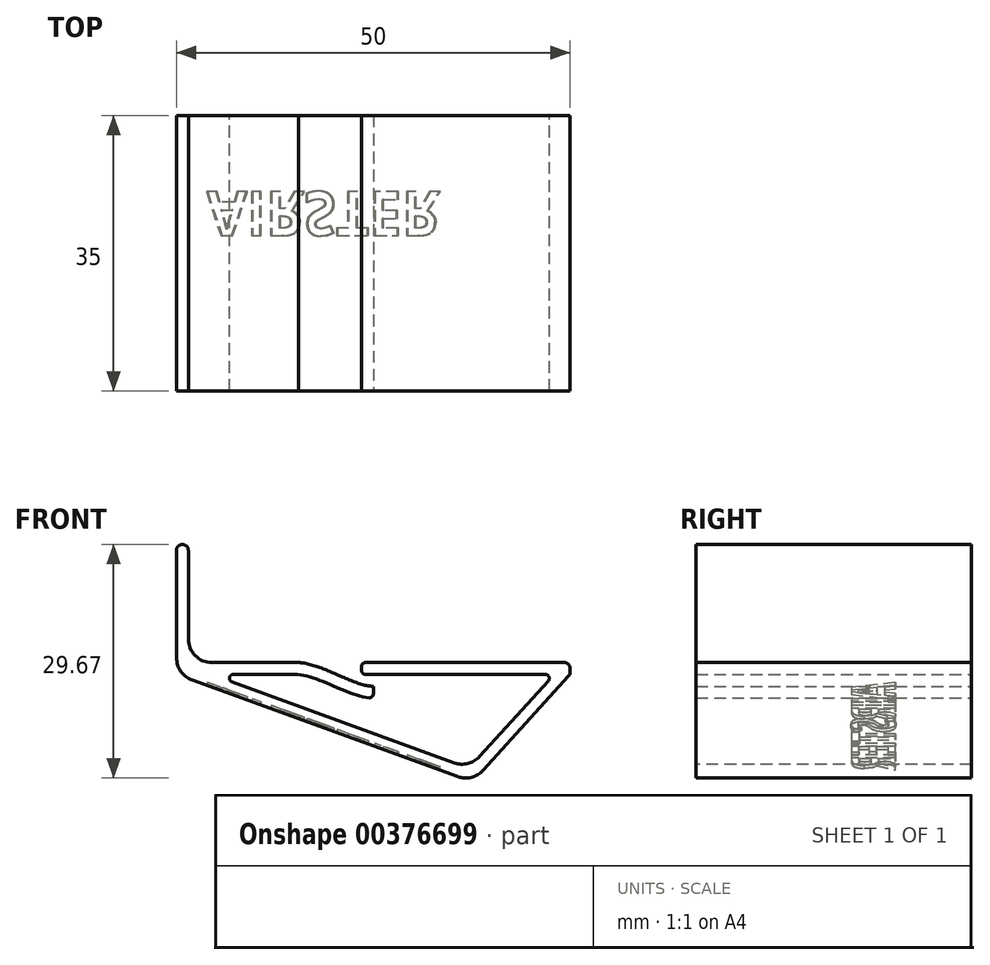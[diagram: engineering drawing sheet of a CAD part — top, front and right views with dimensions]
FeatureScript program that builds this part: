
annotation { "Feature Type Name" : "Feature", "Feature Type Description" : "" }
export const myFeature = defineFeature(function(context is Context, id is Id, definition is map)
    precondition{}
    {
        {
            var Q0;
            Q0=qCreatedBy(makeId("Front.planeOp"),FACE);
            var sketch = newSketch(context, id + "F0", { "sketchPlane" : qUnion([Q0])});
            skLineSegment(sketch, "E0.bottom", {"start": v(0, 1.5) * mm, "end": v(50, 1.5) * mm});
            skLineSegment(sketch, "E0.top", {"start": v(0, 0) * mm, "end": v(50, 0) * mm});
            skLineSegment(sketch, "E0.left", {"start": v(0, 1.5) * mm, "end": v(0, 0) * mm});
            skLineSegment(sketch, "E0.right", {"start": v(50, 1.5) * mm, "end": v(50, 0) * mm});
            skLineSegment(sketch, "E1.bottom", {"start": v(0, 16.5) * mm, "end": v(1.5, 16.5) * mm});
            skLineSegment(sketch, "E1.top", {"start": v(0, 1.5) * mm, "end": v(1.5, 1.5) * mm});
            skLineSegment(sketch, "E1.left", {"start": v(0, 16.5) * mm, "end": v(0, 1.5) * mm});
            skLineSegment(sketch, "E1.right", {"start": v(1.5, 16.5) * mm, "end": v(1.5, 1.5) * mm});
            skFitSpline(sketch, "E2", {"points": [v(25, -3) * mm, v(15, 0) * mm], "startDerivative": vector(-9, 0) * mm, "endDerivative": vector(-9, 0) * mm});
            skLineSegment(sketch, "E3", {"start": v(0, 0) * mm, "end": v(37.59, -13.68) * mm});
            skLineSegment(sketch, "E4", {"start": v(4.39, 0) * mm, "end": v(38.1, -12.27) * mm});
            skLineSegment(sketch, "E5", {"start": v(37.59, -13.68) * mm, "end": v(38.1, -12.27) * mm});
            skLineSegment(sketch, "E6", {"start": v(37.59, -13.68) * mm, "end": v(50, 0) * mm});
            skLineSegment(sketch, "E7", {"start": v(37.15, -11.93) * mm, "end": v(47.97, 0) * mm});
            skLineSegment(sketch, "E8", {"start": v(25, -3) * mm, "end": v(25, 1.5) * mm});
            skLineSegment(sketch, "E9.0", {"start": v(23.5, -1.24) * mm, "end": v(23.5, 1.5) * mm});
            skFitSpline(sketch, "E9.1", {"points": [v(25, -1.5) * mm, v(24.75, -1.5) * mm, v(24.16, -1.44) * mm, v(23.09, -1.13) * mm, v(21.89, -0.68) * mm, v(20.6, -0.13) * mm, v(19.26, 0.45) * mm, v(17.89, 0.97) * mm, v(16.48, 1.38) * mm, v(15.5, 1.5) * mm, v(15, 1.5) * mm]});
            skSolve(sketch);
        }
        {
            var Q0;
            Q0=makeQuery(id+"F0.imprint","IMPRINT",FACE,{"disambiguationData":[TD([[makeQuery(id+"F0.imprint","IMPRINT",EDGE,{"derivedFrom":sQuery(id+"F0.wireOp",EDGE,"E1.bottom")}),-1.0]])]});
            var Q1;
            {var subQ4=sQuery(id+"F0.wireOp",EDGE,"E0.left");Q1=makeQuery(id+"F0.imprint","IMPRINT",FACE,{"disambiguationData":[TD([[makeQuery(id+"F0.imprint","IMPRINT",EDGE,{"derivedFrom":subQ4}),1.0]])]});}
            var Q2;
            {var subQ1=sQuery(id+"F0.wireOp",EDGE,"E2");Q2=makeQuery(id+"F0.imprint","IMPRINT",FACE,{"disambiguationData":[TD([[makeQuery(id+"F0.imprint","IMPRINT",EDGE,{"derivedFrom":subQ1}),-1.0]])]});}
            var Q3;
            {var subQ0=sQuery(id+"F0.wireOp",EDGE,"E8");var subQ1=sQuery(id+"F0.wireOp",EDGE,"E0.bottom");var subQ2=makeQuery(id+"F0.imprint","INTERSECT",VERTEX,{"derivedFrom":[subQ1,subQ0]});Q3=makeQuery(id+"F0.imprint","IMPRINT",FACE,{"disambiguationData":[TD([[makeQuery(id+"F0.imprint","IMPRINT",EDGE,{"disambiguationData":[TD([[subQ2,1.0]])],"derivedFrom":subQ1}),-1.0]])]});}
            var Q4;
            {var subQ0=sQuery(id+"F0.wireOp",EDGE,"E0.right");Q4=makeQuery(id+"F0.imprint","IMPRINT",FACE,{"disambiguationData":[TD([[makeQuery(id+"F0.imprint","IMPRINT",EDGE,{"derivedFrom":subQ0}),-1.0]])]});}
            var Q5;
            {var subQ1=sQuery(id+"F0.wireOp",EDGE,"E5");Q5=makeQuery(id+"F0.imprint","IMPRINT",FACE,{"disambiguationData":[TD([[makeQuery(id+"F0.imprint","IMPRINT",EDGE,{"derivedFrom":subQ1}),-1.0]])]});}
            var Q6;
            {var subQ3=sQuery(id+"F0.wireOp",EDGE,"E3");Q6=makeQuery(id+"F0.imprint","IMPRINT",FACE,{"disambiguationData":[TD([[makeQuery(id+"F0.imprint","IMPRINT",EDGE,{"derivedFrom":subQ3}),1.0]])]});}
            extrude(context, id + "F1", {"entities" : qUnion([Q0, Q1, Q2, Q3, Q4, Q5, Q6]), "depth" : 35 * mm});
        }
        {
            var Q0;
            Q0=makeQuery(id+"F1.opExtrude","SWEPT_EDGE",EDGE,{"disambiguationData":[OSD([sQuery(id+"F0.wireOp",EDGE,"E0.bottom"),sQuery(id+"F0.wireOp",EDGE,"E1.top"),sQuery(id+"F0.wireOp",EDGE,"E1.right")])]});
            var Q1;
            Q1=makeQuery(id+"F1.opExtrude","SWEPT_EDGE",EDGE,{"disambiguationData":[OSD([sQuery(id+"F0.wireOp",EDGE,"E0.top"),sQuery(id+"F0.wireOp",EDGE,"E0.left"),sQuery(id+"F0.wireOp",EDGE,"E3")])]});
            var Q2;
            Q2=makeQuery(id+"F1.opExtrude","SWEPT_EDGE",EDGE,{"disambiguationData":[OSD([sQuery(id+"F0.wireOp",EDGE,"E3"),sQuery(id+"F0.wireOp",EDGE,"E5"),sQuery(id+"F0.wireOp",EDGE,"E6")])]});
            var Q3;
            Q3=makeQuery(id+"F1.opExtrude","SWEPT_EDGE",EDGE,{"disambiguationData":[OSD([sQuery(id+"F0.wireOp",EDGE,"E4"),sQuery(id+"F0.wireOp",EDGE,"E7")])]});
            fillet(context, id + "F2", {"entities" : qUnion([Q0, Q1, Q2, Q3]), "radius" : 3 * mm, "tangentPropagation" : true, "allowEdgeOverflow" : false});
        }
        {
            var Q0;
            Q0=makeQuery(id+"F1.opExtrude","SWEPT_EDGE",EDGE,{"disambiguationData":[OSD([sQuery(id+"F0.wireOp",EDGE,"E0.top"),sQuery(id+"F0.wireOp",EDGE,"E7")])]});
            var Q1;
            Q1=makeQuery(id+"F1.opExtrude","SWEPT_EDGE",EDGE,{"disambiguationData":[OSD([sQuery(id+"F0.wireOp",EDGE,"E0.top"),sQuery(id+"F0.wireOp",EDGE,"E4")])]});
            var Q2;
            Q2=makeQuery(id+"F1.opExtrude","SWEPT_EDGE",EDGE,{"disambiguationData":[OSD([sQuery(id+"F0.wireOp",EDGE,"E0.top"),sQuery(id+"F0.wireOp",EDGE,"aB5ngfBG-Lgge-cUuf-RRZt-Tg2LnY0Fz7UZ")])]});
            var Q3;
            Q3=makeQuery(id+"F1.opExtrude","SWEPT_EDGE",EDGE,{"disambiguationData":[OSD([sQuery(id+"F0.wireOp",EDGE,"aB5ngfBG-Lgge-cUuf-RRZt-Tg2LnY0Fz7UZ"),sQuery(id+"F0.wireOp",EDGE,"E2")])]});
            var Q4;
            Q4=makeQuery(id+"F1.opExtrude","SWEPT_EDGE",EDGE,{"disambiguationData":[OSD([sQuery(id+"F0.wireOp",EDGE,"E0.bottom"),sQuery(id+"F0.wireOp",EDGE,"E9.0")])]});
            fillet(context, id + "F3", {"entities" : qUnion([Q0, Q1, Q2, Q3, Q4]), "radius" : 0.5 * mm, "tangentPropagation" : true, "allowEdgeOverflow" : false});
        }
        {
            var Q0;
            Q0=makeQuery(id+"F1.opExtrude","SWEPT_EDGE",EDGE,{"disambiguationData":[OSD([sQuery(id+"F0.wireOp",EDGE,"E0.top"),sQuery(id+"F0.wireOp",EDGE,"E0.right"),sQuery(id+"F0.wireOp",EDGE,"E6")])]});
            var Q1;
            Q1=makeQuery(id+"F1.opExtrude","SWEPT_EDGE",EDGE,{"disambiguationData":[OSD([sQuery(id+"F0.wireOp",EDGE,"E0.bottom"),sQuery(id+"F0.wireOp",EDGE,"E0.right")])]});
            var Q2;
            Q2=makeQuery(id+"F1.opExtrude","SWEPT_EDGE",EDGE,{"disambiguationData":[OSD([sQuery(id+"F0.wireOp",EDGE,"E1.bottom"),sQuery(id+"F0.wireOp",EDGE,"E1.right")])]});
            var Q3;
            Q3=makeQuery(id+"F1.opExtrude","SWEPT_EDGE",EDGE,{"disambiguationData":[OSD([sQuery(id+"F0.wireOp",EDGE,"E1.bottom"),sQuery(id+"F0.wireOp",EDGE,"E1.left")])]});
            fillet(context, id + "F4", {"entities" : qUnion([Q0, Q1, Q2, Q3]), "radius" : 0.75 * mm, "tangentPropagation" : true, "allowEdgeOverflow" : false});
        }
        {
            var Q0;
            Q0=makeQuery(id+"F1.opExtrude","SWEPT_FACE",FACE,{"disambiguationData":[OSD([sQuery(id+"F0.wireOp",EDGE,"E3")])]});
            var sketch = newSketch(context, id + "F5", { "sketchPlane" : qUnion([Q0])});
            skText(sketch, "E10", { "text": "AIRSTER", "fontName": "OpenSans-Bold.ttf"});
            skPoint(sketch, "E11", {"position": v(36.04, 17.5) * mm});
            const initialGuessF5  = {"E10": [0.00404, 0.00969, 1, 0, 0.00562]};
            skSetInitialGuess(sketch, initialGuessF5);
            skSolve(sketch);
        }
        {
            var Q0;
            Q0 = qSketchRegion(id + "F5", true);
            extrude(context, id + "F6", {"entities" : qUnion([Q0]), "operationType" : NewBodyOperationType.REMOVE, "oppositeDirection" : true, "depth" : 0.4 * mm});
        }
    });
